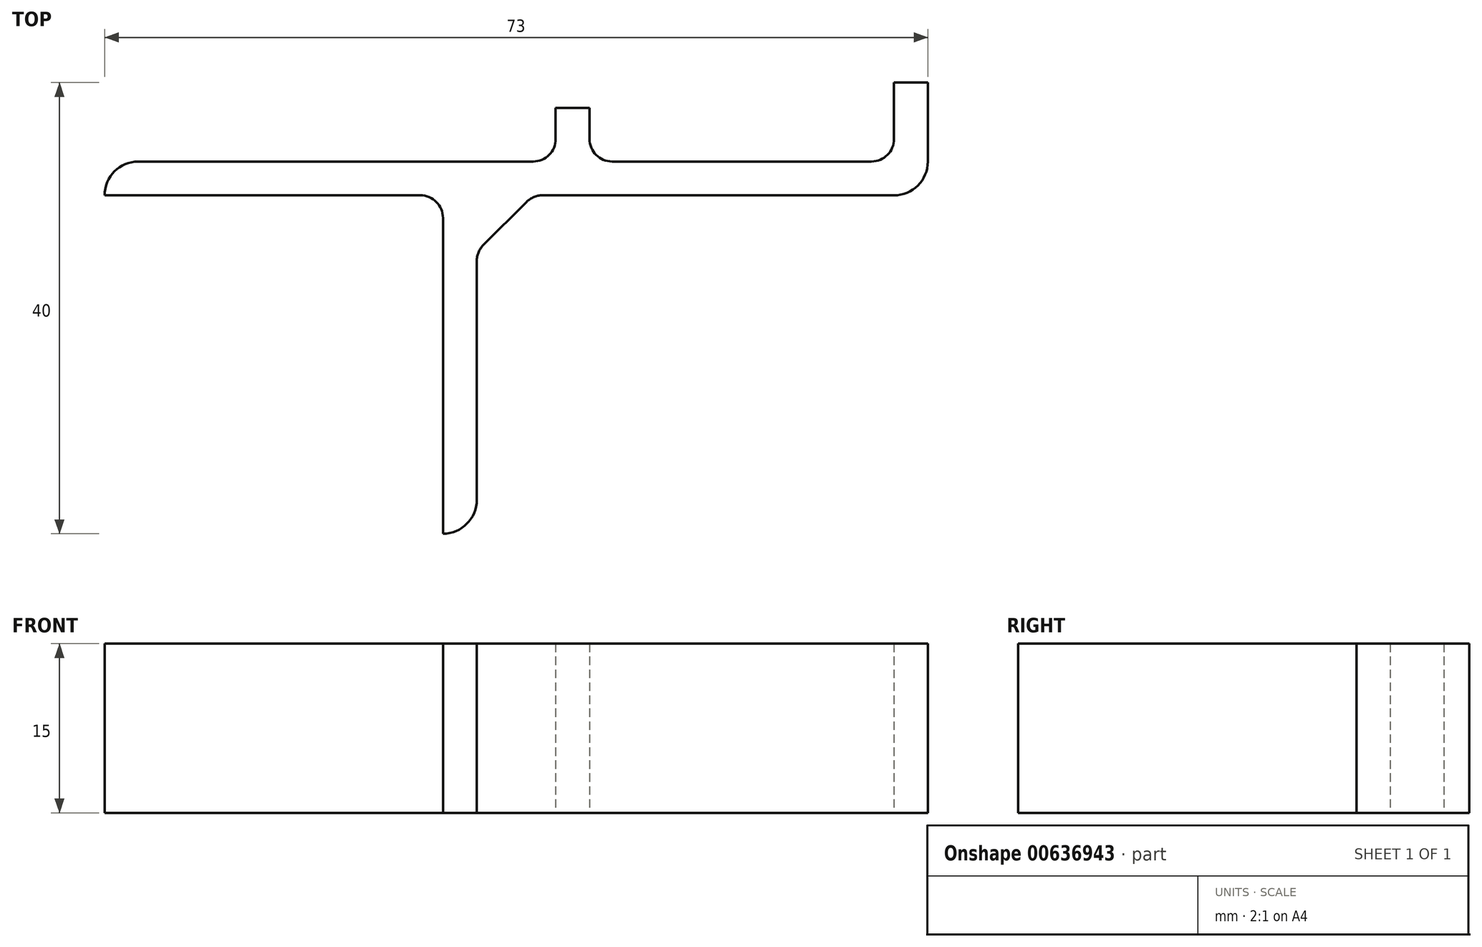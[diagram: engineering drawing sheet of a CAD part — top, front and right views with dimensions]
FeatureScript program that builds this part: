
annotation { "Feature Type Name" : "Feature", "Feature Type Description" : "" }
export const myFeature = defineFeature(function(context is Context, id is Id, definition is map)
    precondition{}
    {
        {
            var Q0;
            Q0=qCreatedBy(makeId("Top.planeOp"),FACE);
            var sketch = newSketch(context, id + "F0", { "sketchPlane" : qUnion([Q0])});
            skLineSegment(sketch, "E0.bottom", {"start": v(0, 0) * mm, "end": v(-30, 0) * mm});
            skLineSegment(sketch, "E0.top", {"start": v(0, -3) * mm, "end": v(-30, -3) * mm});
            skLineSegment(sketch, "E0.left", {"start": v(0, 0) * mm, "end": v(0, -3) * mm});
            skLineSegment(sketch, "E0.right", {"start": v(-30, 0) * mm, "end": v(-30, -3) * mm});
            skLineSegment(sketch, "E1.bottom", {"start": v(0, 0) * mm, "end": v(3, 0) * mm});
            skLineSegment(sketch, "E1.top", {"start": v(0, -33) * mm, "end": v(3, -33) * mm});
            skLineSegment(sketch, "E1.left", {"start": v(0, 0) * mm, "end": v(0, -33) * mm});
            skLineSegment(sketch, "E1.right", {"start": v(3, 0) * mm, "end": v(3, -33) * mm});
            skLineSegment(sketch, "E2.bottom", {"start": v(3, 0) * mm, "end": v(43, 0) * mm});
            skLineSegment(sketch, "E2.top", {"start": v(3, -3) * mm, "end": v(43, -3) * mm});
            skLineSegment(sketch, "E2.left", {"start": v(3, 0) * mm, "end": v(3, -3) * mm});
            skLineSegment(sketch, "E2.right", {"start": v(43, 0) * mm, "end": v(43, -3) * mm});
            skLineSegment(sketch, "E3.bottom", {"start": v(43, 0) * mm, "end": v(40, 0) * mm});
            skLineSegment(sketch, "E3.top", {"start": v(43, 7) * mm, "end": v(40, 7) * mm});
            skLineSegment(sketch, "E3.left", {"start": v(43, 0) * mm, "end": v(43, 7) * mm});
            skLineSegment(sketch, "E3.right", {"start": v(40, 0) * mm, "end": v(40, 7) * mm});
            skLineSegment(sketch, "E4.bottom", {"start": v(10, 0) * mm, "end": v(13, 0) * mm});
            skLineSegment(sketch, "E4.top", {"start": v(10, 4.76) * mm, "end": v(13, 4.76) * mm});
            skLineSegment(sketch, "E4.left", {"start": v(10, 0) * mm, "end": v(10, 4.76) * mm});
            skLineSegment(sketch, "E4.right", {"start": v(13, 0) * mm, "end": v(13, 4.76) * mm});
            skSolve(sketch);
        }
        {
            var Q0;
            Q0 = qSketchRegion(id + "F0", true);
            extrude(context, id + "F1", {"entities" : qUnion([Q0]), "depth" : 15 * mm, "offsetDistance" : 25 * mm});
        }
        {
            var Q0;
            Q0=makeQuery(id+"F1.opExtrude","SWEPT_EDGE",EDGE,{"disambiguationData":[OSD([sQuery(id+"F0.wireOp",EDGE,"E0.top"),sQuery(id+"F0.wireOp",EDGE,"E1.left")])]});
            fillet(context, id + "F2", {"entities" : qUnion([Q0]), "radius" : 2 * mm, "tangentPropagation" : true, "allowEdgeOverflow" : false});
        }
        {
            var Q0;
            Q0=makeQuery(id+"F1.opExtrude","SWEPT_EDGE",EDGE,{"disambiguationData":[OSD([sQuery(id+"F0.wireOp",EDGE,"E1.right"),sQuery(id+"F0.wireOp",EDGE,"E2.top"),sQuery(id+"F0.wireOp",EDGE,"E2.left")])]});
            chamfer(context, id + "F3", {"entities" : qUnion([Q0]), "width" : 5 * mm, "tangentPropagation" : true});
        }
        {
            var Q0;
            Q0=makeQuery(id+"F1.opExtrude","SWEPT_EDGE",EDGE,{"disambiguationData":[OSD([sQuery(id+"F0.wireOp",EDGE,"E2.bottom"),sQuery(id+"F0.wireOp",EDGE,"E4.bottom"),sQuery(id+"F0.wireOp",EDGE,"E4.right")])]});
            var Q1;
            Q1=makeQuery(id+"F1.opExtrude","SWEPT_EDGE",EDGE,{"disambiguationData":[OSD([sQuery(id+"F0.wireOp",EDGE,"E2.bottom"),sQuery(id+"F0.wireOp",EDGE,"E3.bottom"),sQuery(id+"F0.wireOp",EDGE,"E3.right")])]});
            var Q2;
            Q2=makeQuery(id+"F1.opExtrude","SWEPT_EDGE",EDGE,{"disambiguationData":[OSD([sQuery(id+"F0.wireOp",EDGE,"E2.bottom"),sQuery(id+"F0.wireOp",EDGE,"E4.bottom"),sQuery(id+"F0.wireOp",EDGE,"E4.left")])]});
            fillet(context, id + "F4", {"entities" : qUnion([Q0, Q1, Q2]), "radius" : 2 * mm, "tangentPropagation" : true, "allowEdgeOverflow" : false});
        }
        {
            var Q0;
            Q0=makeQuery(id+"F1.opExtrude","SWEPT_EDGE",EDGE,{"disambiguationData":[OSD([sQuery(id+"F0.wireOp",EDGE,"E2.top"),sQuery(id+"F0.wireOp",EDGE,"E2.right")])]});
            fillet(context, id + "F5", {"entities" : qUnion([Q0]), "radius" : 3 * mm, "tangentPropagation" : true, "allowEdgeOverflow" : false});
        }
        {
            var Q0;
            Q0=makeQuery(id+"F1.opExtrude","SWEPT_EDGE",EDGE,{"disambiguationData":[OSD([sQuery(id+"F0.wireOp",EDGE,"E0.bottom"),sQuery(id+"F0.wireOp",EDGE,"E0.right")])]});
            fillet(context, id + "F6", {"entities" : qUnion([Q0]), "radius" : 3 * mm, "tangentPropagation" : true, "allowEdgeOverflow" : false});
        }
        {
            var Q0;
            Q0=makeQuery(id+"F1.opExtrude","SWEPT_EDGE",EDGE,{"disambiguationData":[OSD([sQuery(id+"F0.wireOp",EDGE,"E1.top"),sQuery(id+"F0.wireOp",EDGE,"E1.right")])]});
            fillet(context, id + "F7", {"entities" : qUnion([Q0]), "radius" : 3 * mm, "tangentPropagation" : true, "allowEdgeOverflow" : false});
        }
        {
            var Q0;
            {var subQ0=sQuery(id+"F0.wireOp",EDGE,"E2.top");Q0=makeQuery(id+"F3.opChamfer","BLEND_EDGE",EDGE,{"blendedFrom":[makeQuery(id+"F1.opExtrude","SWEPT_EDGE",EDGE,{"disambiguationData":[OSD([sQuery(id+"F0.wireOp",EDGE,"E1.right"),subQ0,sQuery(id+"F0.wireOp",EDGE,"E2.left")])]}),makeQuery(id+"F1.opExtrude","SWEPT_FACE",FACE,{"disambiguationData":[OSD([subQ0])]})],"blendedInto":[makeQuery(id+"F1.opExtrude","SWEPT_FACE",FACE,{"disambiguationData":[OSD([subQ0])]})]});}
            fillet(context, id + "F8", {"entities" : qUnion([Q0]), "radius" : 2 * mm, "tangentPropagation" : true, "allowEdgeOverflow" : false});
        }
        {
            var Q0;
            {var subQ0=sQuery(id+"F0.wireOp",EDGE,"E1.right");Q0=makeQuery(id+"F3.opChamfer","BLEND_EDGE",EDGE,{"blendedFrom":[makeQuery(id+"F1.opExtrude","SWEPT_EDGE",EDGE,{"disambiguationData":[OSD([subQ0,sQuery(id+"F0.wireOp",EDGE,"E2.top"),sQuery(id+"F0.wireOp",EDGE,"E2.left")])]}),makeQuery(id+"F1.opExtrude","SWEPT_FACE",FACE,{"disambiguationData":[OSD([subQ0])]})],"blendedInto":[makeQuery(id+"F1.opExtrude","SWEPT_FACE",FACE,{"disambiguationData":[OSD([subQ0])]})]});}
            fillet(context, id + "F9", {"entities" : qUnion([Q0]), "radius" : 2 * mm, "tangentPropagation" : true, "allowEdgeOverflow" : false});
        }
    });
